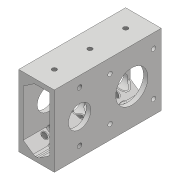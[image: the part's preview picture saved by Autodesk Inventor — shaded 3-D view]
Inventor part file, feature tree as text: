
AUTODESK INVENTOR PART (.ipt)
format: ipt  version: 2018 (Build 220112000, 112)  size: 753,664 bytes
history: native  units: mm
features: sketch x7, hole x5, fillet x4, extrude x3, chamfer x3, other x3, shell x1, reference x1, projected_geometry x1
ambient origin geometry x8: Origin, YZ Plane, XZ Plane, XY Plane, X Axis, Y Axis, Z Axis, Center Point
bodies: Solid1 (feature_tree)
feature tree (28):
  extrude  "Extrusion1"  Depth=25.4mm
  shell  "Shell1"  Thickness=76.2mm
  chamfer  "Chamfer1"  Distance=23.0mm
  chamfer  "Chamfer2"  Distance=50.8mm
  chamfer  "Chamfer3"  Distance=16.0mm
  sketch  "Sketch2"  dims[d4=3.175mm]
  hole  "Hole1"  [1 undecoded]
  hole  "Hole2"  [1 undecoded]
  extrude  "Extrusion2"  Depth=36.0mm
  extrude  "Extrusion3"  Depth=50.8mm
  hole  "Hole4"  [1 undecoded]
  hole  "Hole5"  [1 undecoded]
  fillet  "Fillet1"  Radius=8.0mm
  fillet  "Fillet2"  Radius=3.0mm
  fillet  "Fillet3"  Radius=3.0mm
  hole  "Hole7"  [1 undecoded]
  fillet  "Fillet5"  Radius=14.0mm
  sketch  "Sketch1"  dims[d0=50.8mm d1=25.4mm d2=76.2mm d3=0.0mm]
  sketch  "Sketch3"  dims[d5=31.0mm]
  sketch  "Sketch4"  dims[d6=31.0mm]
  sketch  "Sketch6"  dims[d7=21.0mm]
  sketch  "Sketch7"  dims[d8=3.2mm d9=6.0mm d10=8.0mm d11=22.225mm d12=90.0deg d13=8.0mm d14=20.594885mm]
  reference  "Reference1"
  sketch  "Sketch10"  dims[d15=10.0mm d16=6.0mm d17=6.5mm d18=3.0mm d19=90.0deg d20=8.0mm d21=20.594885mm d22=23.0mm d23=50.8mm d24=0.0mm d25=16.0mm d26=18.0mm d27=50.8mm d28=0.0mm d40=3.242mm d41=100.0mm d42=6.5mm d43=3.0mm d44=90.0deg d45=11.8mm d46=20.594885mm d47=36.0mm d48=3.242mm d49=100.0mm d50=6.5mm d51=3.0mm d52=90.0deg d53=11.8mm d54=20.594885mm d55=50.8mm d56=8.0mm d57=5.5mm d58=45.0deg d59=5.5mm d60=8.0mm d61=45.0deg d62=8.0mm d63=5.5mm d64=45.0deg d68=3.0mm d69=3.0mm d70=1.5mm d86=14.0mm d87=3.242mm d88=8.0mm d89=4.0mm d90=2.0mm d91=90.0deg d92=11.8mm d93=20.594885mm d94=0.5mm]
  projected_geometry  "Projected Loop2"
  parser-record x1  (decoder bookkeeping rows leaked as tree rows — omitted from the tree; the rows remain in map.json)
  other  "AMR_Transm2.iam"
  other  "7804K147_STAINLESS STEEL BALL BEARING:2"
note: 5 required parameter values undecoded (feature->parameter linkage not recoverable at this tier; creation-order binding heuristic only, values carry confidence <= 0.55)
note: 1 file-system path scrubbed to <path> (originals preserved in map.json)
